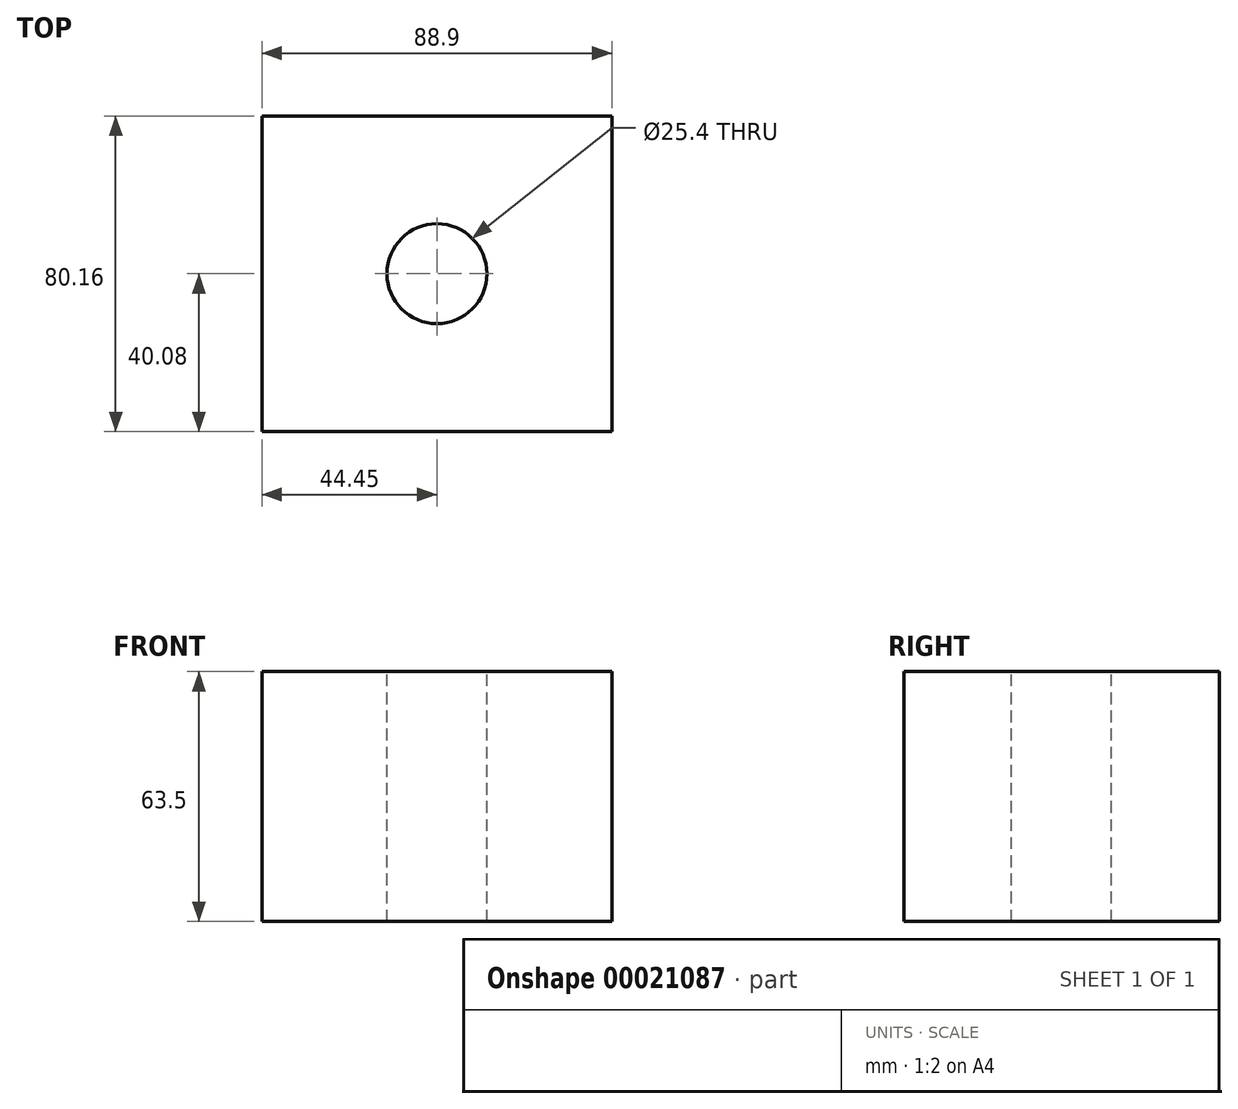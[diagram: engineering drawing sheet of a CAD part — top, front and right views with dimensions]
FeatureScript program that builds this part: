
annotation { "Feature Type Name" : "Feature", "Feature Type Description" : "" }
export const myFeature = defineFeature(function(context is Context, id is Id, definition is map)
    precondition{}
    {
        {
            var Q0;
            Q0=qCreatedBy(makeId("Top.planeOp"),FACE);
            var sketch = newSketch(context, id + "F0", { "sketchPlane" : qUnion([Q0])});
            skLineSegment(sketch, "E0.rect.bottom", {"start": v(44.45, 40.08) * mm, "end": v(-44.45, 40.08) * mm});
            skLineSegment(sketch, "E0.rect.top", {"start": v(44.45, -40.08) * mm, "end": v(-44.45, -40.08) * mm});
            skLineSegment(sketch, "E0.rect.left", {"start": v(44.45, 40.08) * mm, "end": v(44.45, -40.08) * mm});
            skLineSegment(sketch, "E0.rect.right", {"start": v(-44.45, 40.08) * mm, "end": v(-44.45, -40.08) * mm});
            skPoint(sketch, "E0.rect.middle", {"position": v(0, 0) * mm});
            skSolve(sketch);
        }
        {
            var Q0;
            Q0=makeQuery(id+"F0.imprint","IMPRINT",FACE,{"disambiguationData":[TD([[makeQuery(id+"F0.imprint","IMPRINT",EDGE,{"derivedFrom":sQuery(id+"F0.wireOp",EDGE,"E0.rect.bottom")}),1.0]])]});
            extrude(context, id + "F1", {"entities" : qUnion([Q0]), "depth" : 63.5 * mm});
        }
        {
            var Q0;
            Q0=makeQuery(id+"F1.opExtrude","CAP_FACE",FACE,{"disambiguationData":[OSD([sQuery(id+"F0.wireOp",EDGE,"E0.rect.bottom"),sQuery(id+"F0.wireOp",EDGE,"E0.rect.top"),sQuery(id+"F0.wireOp",EDGE,"E0.rect.left"),sQuery(id+"F0.wireOp",EDGE,"E0.rect.right")])],"isStart":false});
            var sketch = newSketch(context, id + "F2", { "sketchPlane" : qUnion([Q0])});
            skPoint(sketch, "E1", {"position": v(0, 0) * mm});
            skSolve(sketch);
        }
        {
            var Q0;
            Q0=sQuery(id+"F2.wireOp",VERTEX,"E1");
            var Q1;
            Q1=makeQuery(id+"F1.opExtrude","SWEPT_BODY",BODY,{"disambiguationData":[OSD([sQuery(id+"F0.wireOp",EDGE,"E0.rect.bottom"),sQuery(id+"F0.wireOp",EDGE,"E0.rect.top"),sQuery(id+"F0.wireOp",EDGE,"E0.rect.left"),sQuery(id+"F0.wireOp",EDGE,"E0.rect.right")])]});
            hole(context, id + "F3", {"style" : HoleStyle.SIMPLE, "holeDiameter" : 25.4 * mm, "endStyle" : HoleEndStyle.THROUGH, "locations" : qUnion([Q0]), "scope" : qUnion([Q1])});
        }
    });
